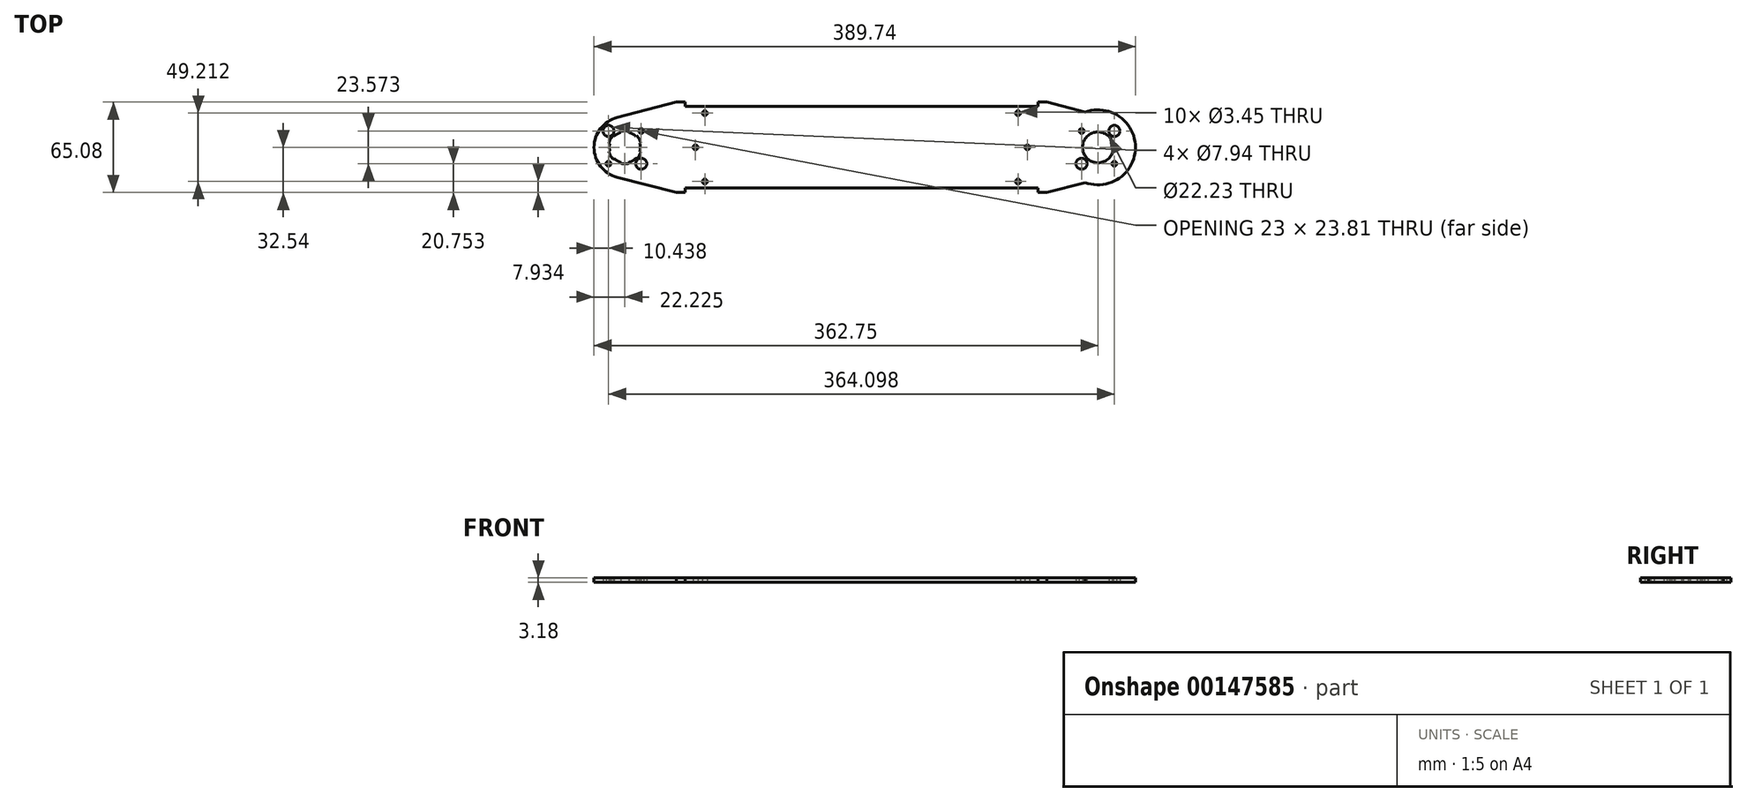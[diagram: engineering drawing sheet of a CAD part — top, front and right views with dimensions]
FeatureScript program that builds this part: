
annotation { "Feature Type Name" : "Feature", "Feature Type Description" : "" }
export const myFeature = defineFeature(function(context is Context, id is Id, definition is map)
    precondition{}
    {
        {
            var Q0;
            Q0=qCreatedBy(makeId("Top.planeOp"),FACE);
            var sketch = newSketch(context, id + "F0", { "sketchPlane" : qUnion([Q0])});
            skPoint(sketch, "E0.rect.middle", {"position": v(0, 0) * mm});
            skCircle(sketch, "E1", {"center": v(0, 0) * mm, "radius": 11.11 * mm});
            skLineSegment(sketch, "E2.bottom", {"start": v(11.79, 11.79) * mm, "end": v(-11.79, 11.79) * mm, "construction": true});
            skLineSegment(sketch, "E2.left", {"start": v(11.79, 11.79) * mm, "end": v(11.79, -11.79) * mm, "construction": true});
            skLineSegment(sketch, "E2.right", {"start": v(-11.79, 11.79) * mm, "end": v(-11.79, -11.79) * mm, "construction": true});
            skCircle(sketch, "E3", {"center": v(-11.79, 11.79) * mm, "radius": 1.73 * mm});
            skCircle(sketch, "E4", {"center": v(11.79, 11.79) * mm, "radius": 3.97 * mm});
            skCircle(sketch, "E5", {"center": v(11.79, -11.79) * mm, "radius": 1.73 * mm});
            skCircle(sketch, "E6", {"center": v(-11.79, -11.79) * mm, "radius": 3.97 * mm});
            skArc(sketch, "E7", {"start": v(-346.1, 21.51) * mm, "mid": v(-362.75, 0) * mm, "end": v(-346.1, -21.51) * mm});
            skLineSegment(sketch, "E8.bottom", {"start": v(-352.31, 11.79) * mm, "end": v(-328.74, 11.79) * mm, "construction": true});
            skLineSegment(sketch, "E8.top", {"start": v(-352.31, -11.79) * mm, "end": v(-328.74, -11.79) * mm, "construction": true});
            skLineSegment(sketch, "E8.left", {"start": v(-352.31, 11.79) * mm, "end": v(-352.31, -11.79) * mm, "construction": true});
            skLineSegment(sketch, "E8.right", {"start": v(-328.74, 11.79) * mm, "end": v(-328.74, -11.79) * mm, "construction": true});
            skCircle(sketch, "E9", {"center": v(-328.74, 11.79) * mm, "radius": 1.73 * mm});
            skCircle(sketch, "E10", {"center": v(-340.53, 0) * mm, "radius": 11.11 * mm});
            skCircle(sketch, "E11", {"center": v(-352.31, 11.79) * mm, "radius": 3.97 * mm});
            skCircle(sketch, "E12", {"center": v(-352.31, -11.79) * mm, "radius": 1.73 * mm});
            skCircle(sketch, "E13", {"center": v(-328.74, -11.79) * mm, "radius": 3.97 * mm});
            skLineSegment(sketch, "E14", {"start": v(0, 0) * mm, "end": v(-340.53, 0) * mm, "construction": true});
            skLineSegment(sketch, "E15", {"start": v(-346.1, -21.51) * mm, "end": v(-303.61, -32.54) * mm});
            skLineSegment(sketch, "E16", {"start": v(-346.1, 21.51) * mm, "end": v(-303.61, 32.54) * mm});
            skLineSegment(sketch, "E17", {"start": v(-297.26, -29.37) * mm, "end": v(-43.26, -29.37) * mm});
            skLineSegment(sketch, "E18", {"start": v(-297.26, 29.37) * mm, "end": v(-43.26, 29.37) * mm});
            skLineSegment(sketch, "E19", {"start": v(-297.26, 32.54) * mm, "end": v(-297.26, 29.37) * mm});
            skLineSegment(sketch, "E20", {"start": v(-297.26, 32.54) * mm, "end": v(-303.61, 32.54) * mm});
            skLineSegment(sketch, "E21", {"start": v(-297.26, -29.37) * mm, "end": v(-297.26, -32.54) * mm});
            skLineSegment(sketch, "E22", {"start": v(-297.26, -32.54) * mm, "end": v(-303.61, -32.54) * mm});
            skLineSegment(sketch, "E23", {"start": v(-43.26, -29.37) * mm, "end": v(-43.26, -32.54) * mm});
            skLineSegment(sketch, "E24", {"start": v(-43.26, -32.54) * mm, "end": v(-36.91, -32.54) * mm});
            skLineSegment(sketch, "E25", {"start": v(-43.26, 29.37) * mm, "end": v(-43.26, 32.54) * mm});
            skLineSegment(sketch, "E26", {"start": v(-43.26, 32.54) * mm, "end": v(-36.91, 32.54) * mm});
            skLineSegment(sketch, "E27", {"start": v(-36.91, -32.54) * mm, "end": v(-9.23, -25.36) * mm});
            skLineSegment(sketch, "E28", {"start": v(-9.23, 25.36) * mm, "end": v(-36.91, 32.54) * mm});
            skLineSegment(sketch, "E29", {"start": v(-297.26, 29.37) * mm, "end": v(-297.26, 24.6) * mm, "construction": true});
            skLineSegment(sketch, "E30", {"start": v(-297.26, 24.6) * mm, "end": v(-282.98, 24.6) * mm, "construction": true});
            skLineSegment(sketch, "E31", {"start": v(-297.26, -29.37) * mm, "end": v(-297.26, -24.6) * mm, "construction": true});
            skLineSegment(sketch, "E32", {"start": v(-297.26, -24.6) * mm, "end": v(-282.98, -24.6) * mm, "construction": true});
            skLineSegment(sketch, "E33", {"start": v(-43.26, -29.37) * mm, "end": v(-43.26, -24.6) * mm, "construction": true});
            skLineSegment(sketch, "E34", {"start": v(-43.26, -24.6) * mm, "end": v(-57.55, -24.6) * mm, "construction": true});
            skLineSegment(sketch, "E35", {"start": v(-43.26, 29.37) * mm, "end": v(-43.26, 24.6) * mm, "construction": true});
            skLineSegment(sketch, "E36", {"start": v(-43.26, 24.6) * mm, "end": v(-57.55, 24.6) * mm, "construction": true});
            skCircle(sketch, "E37", {"center": v(-282.98, 24.6) * mm, "radius": 1.73 * mm});
            skCircle(sketch, "E38", {"center": v(-57.55, 24.6) * mm, "radius": 1.73 * mm});
            skCircle(sketch, "E39", {"center": v(-57.55, -24.6) * mm, "radius": 1.73 * mm});
            skCircle(sketch, "E40", {"center": v(-282.98, -24.6) * mm, "radius": 1.73 * mm});
            skLineSegment(sketch, "E41", {"start": v(-11.79, -11.79) * mm, "end": v(11.79, -11.79) * mm, "construction": true});
            skLineSegment(sketch, "E42", {"start": v(-170.26, -29.37) * mm, "end": v(-170.26, 0) * mm, "construction": true});
            skLineSegment(sketch, "E43", {"start": v(-170.26, 0) * mm, "end": v(-170.26, 29.37) * mm, "construction": true});
            skArc(sketch, "E44", {"start": v(-9.23, -25.36) * mm, "mid": v(26.99, 0) * mm, "end": v(-9.23, 25.36) * mm});
            skLineSegment(sketch, "E45", {"start": v(-9.23, 25.36) * mm, "end": v(5.58, 21.51) * mm, "construction": true});
            skLineSegment(sketch, "E46", {"start": v(-9.23, -25.36) * mm, "end": v(5.58, -21.51) * mm, "construction": true});
            skArc(sketch, "E47", {"start": v(5.58, -21.51) * mm, "mid": v(22.23, 0) * mm, "end": v(5.58, 21.51) * mm, "construction": true});
            skLineSegment(sketch, "E48", {"start": v(-328.74, 11.79) * mm, "end": v(-289.73, 11.79) * mm, "construction": true});
            skLineSegment(sketch, "E49", {"start": v(-289.73, 11.79) * mm, "end": v(-289.73, 0) * mm, "construction": true});
            skLineSegment(sketch, "E50", {"start": v(-11.79, 11.79) * mm, "end": v(-50.8, 11.79) * mm, "construction": true});
            skLineSegment(sketch, "E51", {"start": v(-50.8, 11.79) * mm, "end": v(-50.8, 0) * mm, "construction": true});
            skCircle(sketch, "E52", {"center": v(-289.73, 0) * mm, "radius": 1.73 * mm});
            skCircle(sketch, "E53", {"center": v(-50.8, 0) * mm, "radius": 1.73 * mm});
            skCircle(sketch, "E54", {"center": v(11.79, 11.79) * mm, "radius": 5.56 * mm, "construction": true});
            skLineSegment(sketch, "E55", {"start": v(-36.91, 32.54) * mm, "end": v(-36.91, 25.36) * mm, "construction": true});
            skLineSegment(sketch, "E56", {"start": v(-36.91, 25.36) * mm, "end": v(-9.23, 25.36) * mm, "construction": true});
            skSolve(sketch);
        }
        {
            var Q0;
            Q0=qSketchRegion(id+"F0",true);
            extrude(context, id + "F1", {"entities" : qUnion([Q0]), "depth" : 3.17 * mm});
        }
        {
            var Q0;
            Q0=makeQuery(id+"F1.opExtrude","CAP_FACE",FACE,{"disambiguationData":[OSD([sQuery(id+"F0.wireOp",EDGE,"d63eafa0-1946-4b0e-8293-95e246b273c5.rect.bottom"),sQuery(id+"F0.wireOp",EDGE,"d63eafa0-1946-4b0e-8293-95e246b273c5.rect.top"),sQuery(id+"F0.wireOp",EDGE,"5983dcdd-59a7-4b72-80fd-e4567be1ae8a"),sQuery(id+"F0.wireOp",EDGE,"5a538b3e-fc2b-4d64-affd-5d60433388e5"),sQuery(id+"F0.wireOp",EDGE,"72e86de7-b207-474f-aadf-64543fae3f9b"),sQuery(id+"F0.wireOp",EDGE,"1c038800-5bd5-4753-8b38-6da13ef78ef9"),sQuery(id+"F0.wireOp",EDGE,"EbMUZoU6-Ffds-1dNq-SxhE-hPi8oSjhvaod"),sQuery(id+"F0.wireOp",EDGE,"RfgQjzcw-1Izs-lnTa-bWkk-oBHRDQjbZqQC"),sQuery(id+"F0.wireOp",EDGE,"1cCQAcjj-TyQA-3DMx-kDix-v5yZVaaGeXVM"),sQuery(id+"F0.wireOp",EDGE,"7KPu8lni-3ZWA-t6oJ-FRoh-C5MB3aVr7E9B"),sQuery(id+"F0.wireOp",EDGE,"bSzr06ES-7M0i-Fw5H-UJmt-4e4EQGRPIe4n"),sQuery(id+"F0.wireOp",EDGE,"WGsr6OjU-OX8l-mawA-7cCc-MfOuMOY06Cp5"),sQuery(id+"F0.wireOp",EDGE,"9mrz1cDN-18gM-20ra-6VCO-jp25g10tvNn2"),sQuery(id+"F0.wireOp",EDGE,"G0uOisy3-Mq6h-PcKh-Zkf4-CVoCvP3Hii1l"),sQuery(id+"F0.wireOp",EDGE,"1ae556be-0ab9-4322-b48e-98cf5a741ae0"),sQuery(id+"F0.wireOp",EDGE,"676cd913-43f8-42b3-8cdc-a90136d19ef5"),sQuery(id+"F0.wireOp",EDGE,"xnt2EyF8-ZVyQ-RbWD-GIsP-ThkcyX8ZioIH.bottom"),sQuery(id+"F0.wireOp",EDGE,"xnt2EyF8-ZVyQ-RbWD-GIsP-ThkcyX8ZioIH.top"),sQuery(id+"F0.wireOp",EDGE,"xnt2EyF8-ZVyQ-RbWD-GIsP-ThkcyX8ZioIH.left"),sQuery(id+"F0.wireOp",EDGE,"E1"),sQuery(id+"F0.wireOp",EDGE,"Jo9pZc7T-t0kF-vjz1-dNbX-L65bwNqtrrdz"),sQuery(id+"F0.wireOp",EDGE,"lEYoY9t7-PMOS-SVp6-xfnB-Xp9WdWMCDdum"),sQuery(id+"F0.wireOp",EDGE,"s7aM02SC-9XQ7-dueL-DqMg-ZFuJqOofj9mt"),sQuery(id+"F0.wireOp",EDGE,"deKa9ngt-XMq2-GGkr-SZIa-KlyN0U5bcCDe"),sQuery(id+"F0.wireOp",EDGE,"E3"),sQuery(id+"F0.wireOp",EDGE,"E4"),sQuery(id+"F0.wireOp",EDGE,"E5"),sQuery(id+"F0.wireOp",EDGE,"E6"),sQuery(id+"F0.wireOp",EDGE,"E7"),sQuery(id+"F0.wireOp",EDGE,"E9"),sQuery(id+"F0.wireOp",EDGE,"E10"),sQuery(id+"F0.wireOp",EDGE,"E11"),sQuery(id+"F0.wireOp",EDGE,"E12"),sQuery(id+"F0.wireOp",EDGE,"E13")])],"isStart":true});
            var sketch = newSketch(context, id + "F2", { "sketchPlane" : qUnion([Q0])});
            skLineSegment(sketch, "E57", {"start": v(-340.53, 0) * mm, "end": v(-350.15, -5.56) * mm, "construction": true});
            skArc(sketch, "E58", {"start": v(-351.26, -2.88) * mm, "mid": v(-350.15, -5.56) * mm, "end": v(-348.38, -7.86) * mm});
            skLineSegment(sketch, "E59", {"start": v(-340.53, 0) * mm, "end": v(-348.38, -7.86) * mm, "construction": true});
            skLineSegment(sketch, "E60", {"start": v(-340.53, 0) * mm, "end": v(-351.26, -2.88) * mm, "construction": true});
            skLineSegment(sketch, "E61", {"start": v(-348.38, -7.86) * mm, "end": v(-348.94, -8.42) * mm});
            skLineSegment(sketch, "E62", {"start": v(-351.26, -2.88) * mm, "end": v(-352.03, -3.08) * mm});
            skArc(sketch, "E63", {"start": v(-352.03, -3.08) * mm, "mid": v(-350.84, -5.95) * mm, "end": v(-348.94, -8.42) * mm});
            skLineSegment(sketch, "E64", {"start": v(-340.53, 0) * mm, "end": v(-351.64, 0) * mm, "construction": true});
            skSolve(sketch);
        }
        {
            var Q0;
            Q0=qSketchRegion(id+"F2",true);
            var Q1;
            Q1=makeQuery(id+"F1.opExtrude","CAP_FACE",FACE,{"disambiguationData":[OSD([sQuery(id+"F0.wireOp",EDGE,"d63eafa0-1946-4b0e-8293-95e246b273c5.rect.bottom"),sQuery(id+"F0.wireOp",EDGE,"d63eafa0-1946-4b0e-8293-95e246b273c5.rect.top"),sQuery(id+"F0.wireOp",EDGE,"5983dcdd-59a7-4b72-80fd-e4567be1ae8a"),sQuery(id+"F0.wireOp",EDGE,"5a538b3e-fc2b-4d64-affd-5d60433388e5"),sQuery(id+"F0.wireOp",EDGE,"72e86de7-b207-474f-aadf-64543fae3f9b"),sQuery(id+"F0.wireOp",EDGE,"1c038800-5bd5-4753-8b38-6da13ef78ef9"),sQuery(id+"F0.wireOp",EDGE,"EbMUZoU6-Ffds-1dNq-SxhE-hPi8oSjhvaod"),sQuery(id+"F0.wireOp",EDGE,"RfgQjzcw-1Izs-lnTa-bWkk-oBHRDQjbZqQC"),sQuery(id+"F0.wireOp",EDGE,"1cCQAcjj-TyQA-3DMx-kDix-v5yZVaaGeXVM"),sQuery(id+"F0.wireOp",EDGE,"7KPu8lni-3ZWA-t6oJ-FRoh-C5MB3aVr7E9B"),sQuery(id+"F0.wireOp",EDGE,"bSzr06ES-7M0i-Fw5H-UJmt-4e4EQGRPIe4n"),sQuery(id+"F0.wireOp",EDGE,"WGsr6OjU-OX8l-mawA-7cCc-MfOuMOY06Cp5"),sQuery(id+"F0.wireOp",EDGE,"9mrz1cDN-18gM-20ra-6VCO-jp25g10tvNn2"),sQuery(id+"F0.wireOp",EDGE,"G0uOisy3-Mq6h-PcKh-Zkf4-CVoCvP3Hii1l"),sQuery(id+"F0.wireOp",EDGE,"1ae556be-0ab9-4322-b48e-98cf5a741ae0"),sQuery(id+"F0.wireOp",EDGE,"676cd913-43f8-42b3-8cdc-a90136d19ef5"),sQuery(id+"F0.wireOp",EDGE,"xnt2EyF8-ZVyQ-RbWD-GIsP-ThkcyX8ZioIH.bottom"),sQuery(id+"F0.wireOp",EDGE,"xnt2EyF8-ZVyQ-RbWD-GIsP-ThkcyX8ZioIH.top"),sQuery(id+"F0.wireOp",EDGE,"xnt2EyF8-ZVyQ-RbWD-GIsP-ThkcyX8ZioIH.left"),sQuery(id+"F0.wireOp",EDGE,"E1"),sQuery(id+"F0.wireOp",EDGE,"Jo9pZc7T-t0kF-vjz1-dNbX-L65bwNqtrrdz"),sQuery(id+"F0.wireOp",EDGE,"lEYoY9t7-PMOS-SVp6-xfnB-Xp9WdWMCDdum"),sQuery(id+"F0.wireOp",EDGE,"s7aM02SC-9XQ7-dueL-DqMg-ZFuJqOofj9mt"),sQuery(id+"F0.wireOp",EDGE,"deKa9ngt-XMq2-GGkr-SZIa-KlyN0U5bcCDe"),sQuery(id+"F0.wireOp",EDGE,"E3"),sQuery(id+"F0.wireOp",EDGE,"E4"),sQuery(id+"F0.wireOp",EDGE,"E5"),sQuery(id+"F0.wireOp",EDGE,"E6"),sQuery(id+"F0.wireOp",EDGE,"E7"),sQuery(id+"F0.wireOp",EDGE,"E9"),sQuery(id+"F0.wireOp",EDGE,"E10"),sQuery(id+"F0.wireOp",EDGE,"E11"),sQuery(id+"F0.wireOp",EDGE,"E12"),sQuery(id+"F0.wireOp",EDGE,"E13")])],"isStart":false});
            extrude(context, id + "F3", {"entities" : qUnion([Q0]), "operationType" : NewBodyOperationType.REMOVE, "endBound" : BoundingType.UP_TO_SURFACE, "oppositeDirection" : true, "endBoundEntityFace" : qUnion([Q1]), "depth" : 25.4 * mm});
        }
        {
            var Q0;
            Q0=makeQuery(id+"F3.boolean.opBoolean","COPY",FACE,{"derivedFrom":makeQuery(id+"F3.opExtrude","SWEPT_FACE",FACE,{"disambiguationData":[OSD([sQuery(id+"F2.wireOp",EDGE,"E61")])]})});
            var Q1;
            Q1=makeQuery(id+"F3.boolean.opBoolean","COPY",FACE,{"derivedFrom":makeQuery(id+"F3.opExtrude","SWEPT_FACE",FACE,{"disambiguationData":[OSD([sQuery(id+"F2.wireOp",EDGE,"E63")])]})});
            var Q2;
            Q2=makeQuery(id+"F3.boolean.opBoolean","COPY",FACE,{"derivedFrom":makeQuery(id+"F3.opExtrude","SWEPT_FACE",FACE,{"disambiguationData":[OSD([sQuery(id+"F2.wireOp",EDGE,"E62")])]})});
            var Q3;
            Q3=makeQuery(id+"F1.opExtrude","SWEPT_FACE",FACE,{"disambiguationData":[OSD([sQuery(id+"F0.wireOp",EDGE,"E10")])]});
            circularPattern(context, id + "F4", {"patternType" : PatternType.FACE, "faces" : qUnion([Q0, Q1, Q2]), "axis" : qUnion([Q3]), "angle" : 60 * degree, "instanceCount" : 6});
        }
    });
